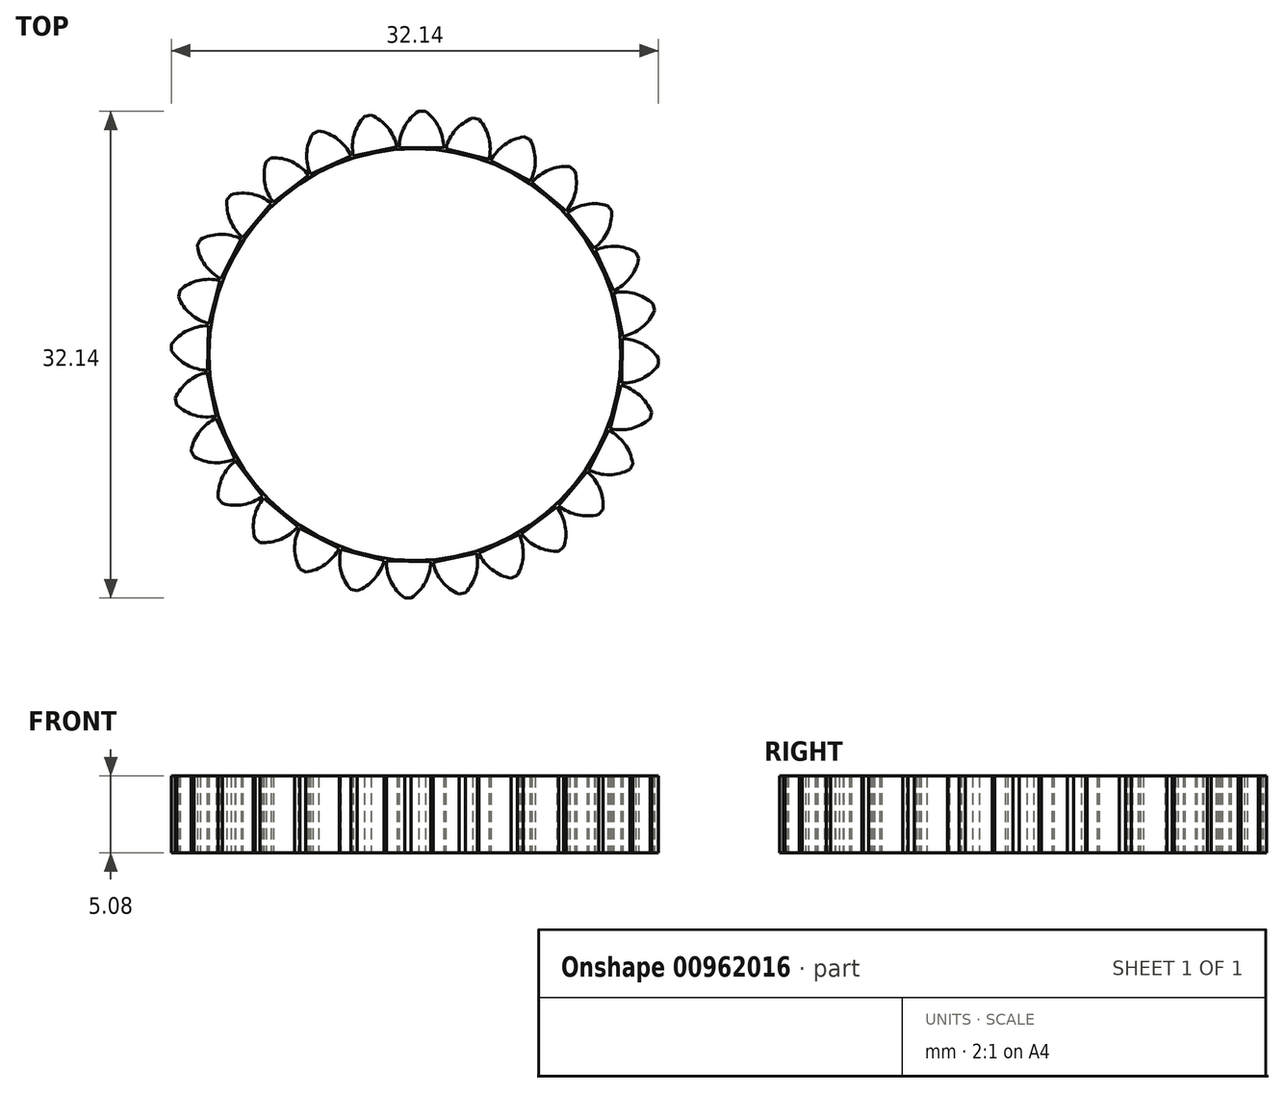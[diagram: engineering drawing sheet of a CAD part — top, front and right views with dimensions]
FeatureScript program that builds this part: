
annotation { "Feature Type Name" : "Feature", "Feature Type Description" : "" }
export const myFeature = defineFeature(function(context is Context, id is Id, definition is map)
    precondition{}
    {
        {
            var Q0;
            Q0=qCreatedBy(makeId("Top.planeOp"),FACE);
            var sketch = newSketch(context, id + "F0", { "sketchPlane" : qUnion([Q0])});
            skCircle(sketch, "E0", {"center": v(0, 0) * mm, "radius": 13.59 * mm});
            skLineSegment(sketch, "E1", {"start": v(0, 13.59) * mm, "end": v(0, -13.59) * mm});
            skLineSegment(sketch, "E2", {"start": v(-13.59, 0) * mm, "end": v(13.59, 0) * mm});
            skSolve(sketch);
        }
        {
            var Q0;
            Q0=qCreatedBy(makeId("Top.planeOp"),FACE);
            var sketch = newSketch(context, id + "F1", { "sketchPlane" : qUnion([Q0])});
            skArc(sketch, "E3", {"start": v(0.25, 16.07) * mm, "mid": v(-0.68, 15.04) * mm, "end": v(-1.04, 13.7) * mm});
            skArc(sketch, "E4", {"start": v(1.9, 13.64) * mm, "mid": v(1.59, 15) * mm, "end": v(0.68, 16.07) * mm});
            skLineSegment(sketch, "E5", {"start": v(-1.04, 13.7) * mm, "end": v(1.9, 13.64) * mm});
            skLineSegment(sketch, "E6", {"start": v(0.43, 13.67) * mm, "end": v(0.47, 16.07) * mm});
            skLineSegment(sketch, "E7", {"start": v(0.25, 16.07) * mm, "end": v(0.68, 16.07) * mm});
            skSolve(sketch);
        }
        {
            var Q0;
            {var subQ0=sQuery(id+"F0.wireOp",EDGE,"E1");var subQ1=sQuery(id+"F0.wireOp",EDGE,"E0");var subQ2=makeQuery(id+"F0.imprint","INTERSECT",VERTEX,{"disambiguationData":[OD(1.0)],"derivedFrom":[subQ1,subQ0]});Q0=makeQuery(id+"F0.imprint","IMPRINT",FACE,{"disambiguationData":[TD([[makeQuery(id+"F0.imprint","IMPRINT",EDGE,{"disambiguationData":[TD([[subQ2,-1.0]])],"derivedFrom":subQ1}),1.0]])]});}
            var Q1;
            {var subQ0=sQuery(id+"F0.wireOp",EDGE,"E1");var subQ1=sQuery(id+"F0.wireOp",EDGE,"E0");var subQ2=makeQuery(id+"F0.imprint","INTERSECT",VERTEX,{"disambiguationData":[OD(1.0)],"derivedFrom":[subQ1,subQ0]});Q1=makeQuery(id+"F0.imprint","IMPRINT",FACE,{"disambiguationData":[TD([[makeQuery(id+"F0.imprint","IMPRINT",EDGE,{"disambiguationData":[TD([[subQ2,1.0]])],"derivedFrom":subQ1}),1.0]])]});}
            var Q2;
            {var subQ0=sQuery(id+"F0.wireOp",EDGE,"E1");var subQ1=sQuery(id+"F0.wireOp",EDGE,"E0");var subQ2=makeQuery(id+"F0.imprint","INTERSECT",VERTEX,{"disambiguationData":[OD(0.0)],"derivedFrom":[subQ1,subQ0]});Q2=makeQuery(id+"F0.imprint","IMPRINT",FACE,{"disambiguationData":[TD([[makeQuery(id+"F0.imprint","IMPRINT",EDGE,{"disambiguationData":[TD([[subQ2,1.0]])],"derivedFrom":subQ1}),1.0]])]});}
            var Q3;
            {var subQ0=sQuery(id+"F0.wireOp",EDGE,"E1");var subQ1=sQuery(id+"F0.wireOp",EDGE,"E0");var subQ2=makeQuery(id+"F0.imprint","INTERSECT",VERTEX,{"disambiguationData":[OD(0.0)],"derivedFrom":[subQ1,subQ0]});Q3=makeQuery(id+"F0.imprint","IMPRINT",FACE,{"disambiguationData":[TD([[makeQuery(id+"F0.imprint","IMPRINT",EDGE,{"disambiguationData":[TD([[subQ2,-1.0]])],"derivedFrom":subQ1}),1.0]])]});}
            extrude(context, id + "F2", {"entities" : qUnion([Q0, Q1, Q2, Q3]), "depth" : 5.08 * mm, "offsetDistance" : 25.4 * mm});
        }
        {
            var Q0;
            {var subQ0=sQuery(id+"F1.wireOp",EDGE,"E3");Q0=makeQuery(id+"F1.imprint","IMPRINT",FACE,{"disambiguationData":[TD([[makeQuery(id+"F1.imprint","IMPRINT",EDGE,{"derivedFrom":subQ0}),1.0]])]});}
            var Q1;
            {var subQ0=sQuery(id+"F1.wireOp",EDGE,"E4");Q1=makeQuery(id+"F1.imprint","IMPRINT",FACE,{"disambiguationData":[TD([[makeQuery(id+"F1.imprint","IMPRINT",EDGE,{"derivedFrom":subQ0}),1.0]])]});}
            extrude(context, id + "F3", {"entities" : qUnion([Q0, Q1]), "operationType" : NewBodyOperationType.ADD, "depth" : 5.08 * mm, "offsetDistance" : 25.4 * mm});
        }
        {
            var Q0;
            Q0=makeQuery(id+"F3.opExtrude","SWEPT_BODY",BODY,{"disambiguationData":[OSD([sQuery(id+"F1.wireOp",EDGE,"E3"),sQuery(id+"F1.wireOp",EDGE,"E4"),sQuery(id+"F1.wireOp",EDGE,"E5"),sQuery(id+"F1.wireOp",EDGE,"E7")])]});
            var Q1;
            Q1=makeQuery(id+"F2.opExtrude","CAP_EDGE",EDGE,{"disambiguationData":[OSD([sQuery(id+"F0.wireOp",EDGE,"E0")])],"isStart":false});
            circularPattern(context, id + "F4", {"entities" : qUnion([Q0]), "axis" : qUnion([Q1]), "angle" : 360 * degree, "instanceCount" : 28, "equalSpace" : true, "isCentered" : true});
        }
    });
